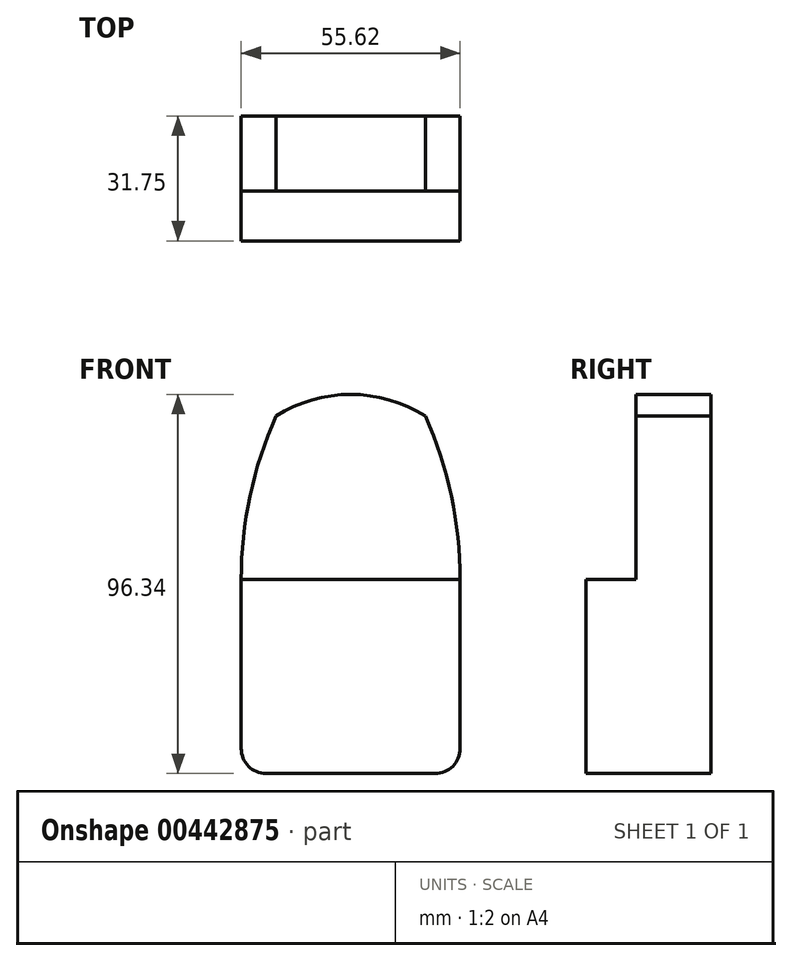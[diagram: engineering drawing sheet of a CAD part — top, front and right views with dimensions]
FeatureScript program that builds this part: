
annotation { "Feature Type Name" : "Feature", "Feature Type Description" : "" }
export const myFeature = defineFeature(function(context is Context, id is Id, definition is map)
    precondition{}
    {
        {
            var Q0;
            Q0=qCreatedBy(makeId("Front.planeOp"),FACE);
            var sketch = newSketch(context, id + "F0", { "sketchPlane" : qUnion([Q0])});
            skLineSegment(sketch, "E0.top", {"start": v(-20.56, -48.8) * mm, "end": v(22.36, -48.8) * mm});
            skLineSegment(sketch, "E0.left", {"start": v(-26.9, 0.5) * mm, "end": v(-26.9, -42.45) * mm});
            skLineSegment(sketch, "E0.right", {"start": v(28.71, 0.5) * mm, "end": v(28.71, -42.45) * mm});
            skPoint(sketch, "E1.visualSharp", {"position": v(-26.9, 8.12) * mm});
            skPoint(sketch, "E2.visualSharp", {"position": v(28.71, 8.12) * mm});
            skPoint(sketch, "E3.visualSharp", {"position": v(28.71, -48.8) * mm});
            skArc(sketch, "E3.filletArc", {"start": v(22.36, -48.8) * mm, "mid": v(26.85, -46.94) * mm, "end": v(28.71, -42.45) * mm});
            skPoint(sketch, "E4.visualSharp", {"position": v(-26.9, -48.8) * mm});
            skArc(sketch, "E4.filletArc", {"start": v(-26.9, -42.45) * mm, "mid": v(-25.05, -46.94) * mm, "end": v(-20.56, -48.8) * mm});
            skArc(sketch, "E5", {"start": v(-18.05, 42) * mm, "mid": v(-24.67, 21.71) * mm, "end": v(-26.9, 0.5) * mm});
            skArc(sketch, "E6", {"start": v(19.85, 42) * mm, "mid": v(0.9, 47.54) * mm, "end": v(-18.05, 42) * mm});
            skLineSegment(sketch, "E7", {"start": v(-26.9, 0.5) * mm, "end": v(28.71, 0.5) * mm});
            skArc(sketch, "E8.MirrorCS", {"start": v(19.85, 42) * mm, "mid": v(26.47, 21.71) * mm, "end": v(28.71, 0.5) * mm});
            skSolve(sketch);
        }
        {
            var Q0;
            Q0=makeQuery(id+"F0.imprint","IMPRINT",FACE,{"disambiguationData":[TD([[makeQuery(id+"F0.imprint","IMPRINT",EDGE,{"derivedFrom":sQuery(id+"F0.wireOp",EDGE,"E5")}),1.0]])]});
            extrude(context, id + "F1", {"entities" : qUnion([Q0]), "depth" : 19.05 * mm});
        }
        {
            var Q0;
            Q0=makeQuery(id+"F0.imprint","IMPRINT",FACE,{"disambiguationData":[TD([[makeQuery(id+"F0.imprint","IMPRINT",EDGE,{"derivedFrom":sQuery(id+"F0.wireOp",EDGE,"E0.top")}),1.0]])]});
            extrude(context, id + "F2", {"entities" : qUnion([Q0]), "operationType" : NewBodyOperationType.ADD, "depth" : 31.75 * mm});
        }
    });
